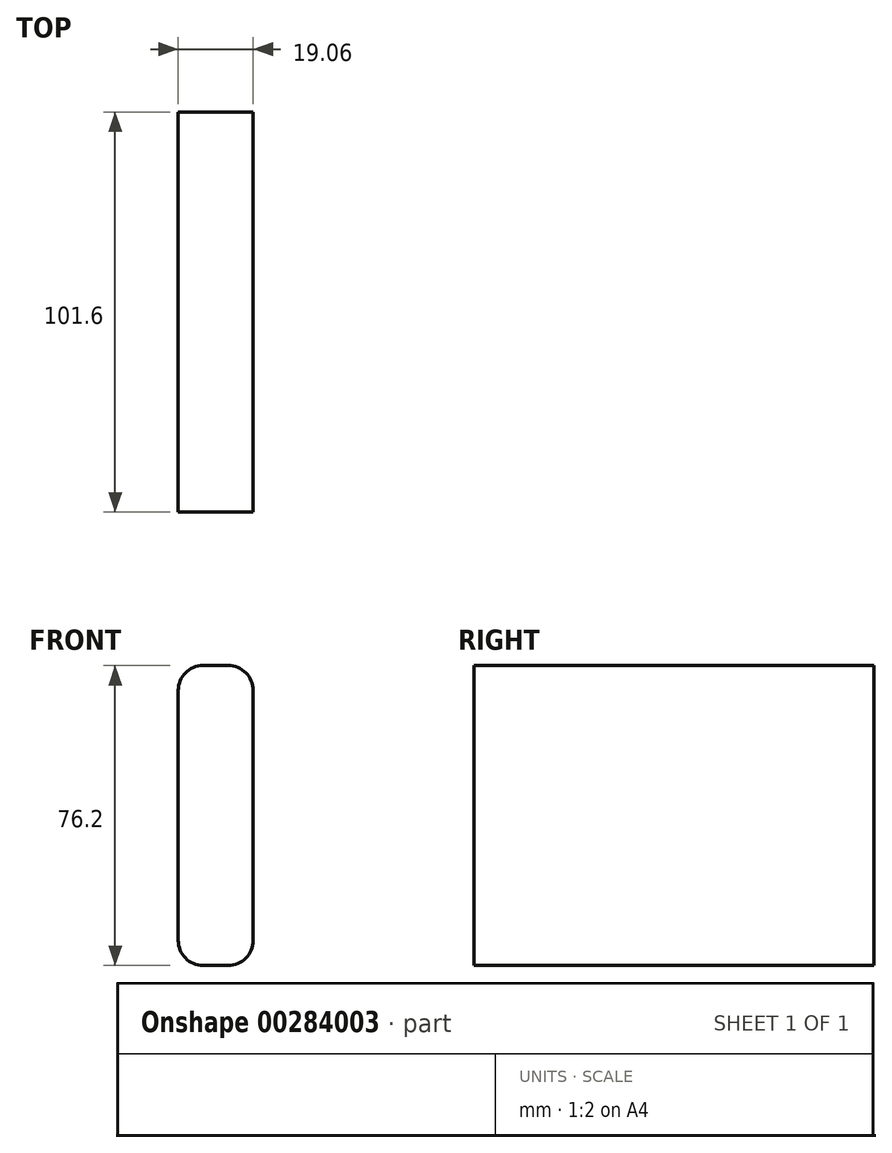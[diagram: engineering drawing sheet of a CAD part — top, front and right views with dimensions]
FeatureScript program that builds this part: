
annotation { "Feature Type Name" : "Feature", "Feature Type Description" : "" }
export const myFeature = defineFeature(function(context is Context, id is Id, definition is map)
    precondition{}
    {
        {
            var Q0;
            Q0=qCreatedBy(makeId("Front.planeOp"),FACE);
            var sketch = newSketch(context, id + "F0", { "sketchPlane" : qUnion([Q0])});
            skLineSegment(sketch, "E0.bottom", {"start": v(3.18, -38.1) * mm, "end": v(-3.17, -38.1) * mm});
            skLineSegment(sketch, "E0.top", {"start": v(3.17, 38.1) * mm, "end": v(-3.18, 38.1) * mm});
            skLineSegment(sketch, "E0.left", {"start": v(9.53, -31.75) * mm, "end": v(9.52, 31.75) * mm});
            skLineSegment(sketch, "E0.right", {"start": v(-9.53, -31.75) * mm, "end": v(-9.53, 31.75) * mm});
            skPoint(sketch, "E0.middle", {"position": v(0, 0) * mm});
            skPoint(sketch, "E1.visualSharp", {"position": v(9.53, -38.1) * mm});
            skArc(sketch, "E1.filletArc", {"start": v(3.18, -38.1) * mm, "mid": v(7.67, -36.24) * mm, "end": v(9.53, -31.75) * mm});
            skPoint(sketch, "E2.visualSharp", {"position": v(9.52, 38.1) * mm});
            skArc(sketch, "E2.filletArc", {"start": v(9.52, 31.75) * mm, "mid": v(7.67, 36.24) * mm, "end": v(3.17, 38.1) * mm});
            skPoint(sketch, "E3.visualSharp", {"position": v(-9.53, 38.1) * mm});
            skArc(sketch, "E3.filletArc", {"start": v(-3.18, 38.1) * mm, "mid": v(-7.67, 36.24) * mm, "end": v(-9.53, 31.75) * mm});
            skPoint(sketch, "E4.visualSharp", {"position": v(-9.52, -38.1) * mm});
            skArc(sketch, "E4.filletArc", {"start": v(-9.52, -31.75) * mm, "mid": v(-7.67, -36.24) * mm, "end": v(-3.17, -38.1) * mm});
            skSolve(sketch);
        }
        {
            var Q0;
            Q0=makeQuery(id+"F0.imprint","IMPRINT",FACE,{"disambiguationData":[TD([[makeQuery(id+"F0.imprint","IMPRINT",EDGE,{"derivedFrom":sQuery(id+"F0.wireOp",EDGE,"E0.bottom")}),-1.0]])]});
            extrude(context, id + "F1", {"entities" : qUnion([Q0]), "depth" : 101.6 * mm});
        }
    });
